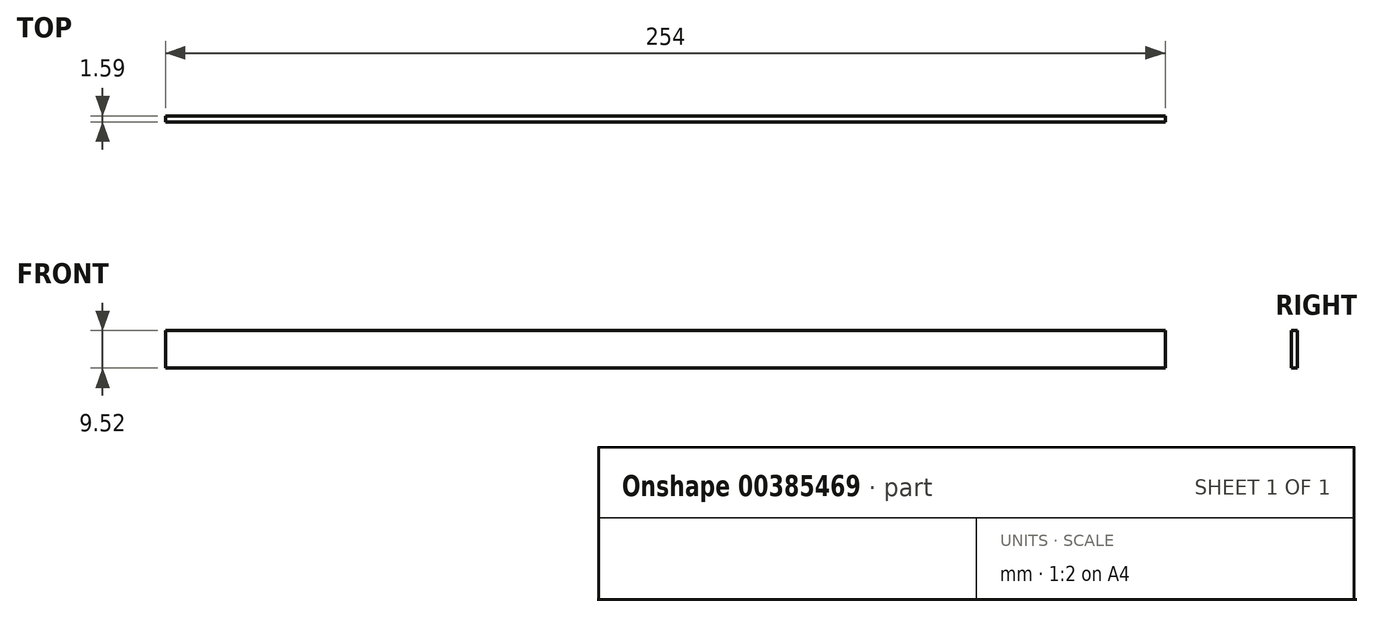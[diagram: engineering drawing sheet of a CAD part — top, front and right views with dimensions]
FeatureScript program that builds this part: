
annotation { "Feature Type Name" : "Feature", "Feature Type Description" : "" }
export const myFeature = defineFeature(function(context is Context, id is Id, definition is map)
    precondition{}
    {
        {
            var Q0;
            Q0=qCreatedBy(makeId("Front.planeOp"),FACE);
            var sketch = newSketch(context, id + "F0", { "sketchPlane" : qUnion([Q0])});
            skLineSegment(sketch, "E0.bottom", {"start": v(127, 4.76) * mm, "end": v(-127, 4.76) * mm});
            skLineSegment(sketch, "E0.top", {"start": v(127, -4.76) * mm, "end": v(-127, -4.76) * mm});
            skLineSegment(sketch, "E0.left", {"start": v(127, 4.76) * mm, "end": v(127, -4.76) * mm});
            skLineSegment(sketch, "E0.right", {"start": v(-127, 4.76) * mm, "end": v(-127, -4.76) * mm});
            skPoint(sketch, "E0.middle", {"position": v(0, 0) * mm});
            skSolve(sketch);
        }
        {
            var Q0;
            Q0 = qSketchRegion(id + "F0", true);
            extrude(context, id + "F1", {"entities" : qUnion([Q0]), "depth" : 1.59 * mm});
        }
    });
